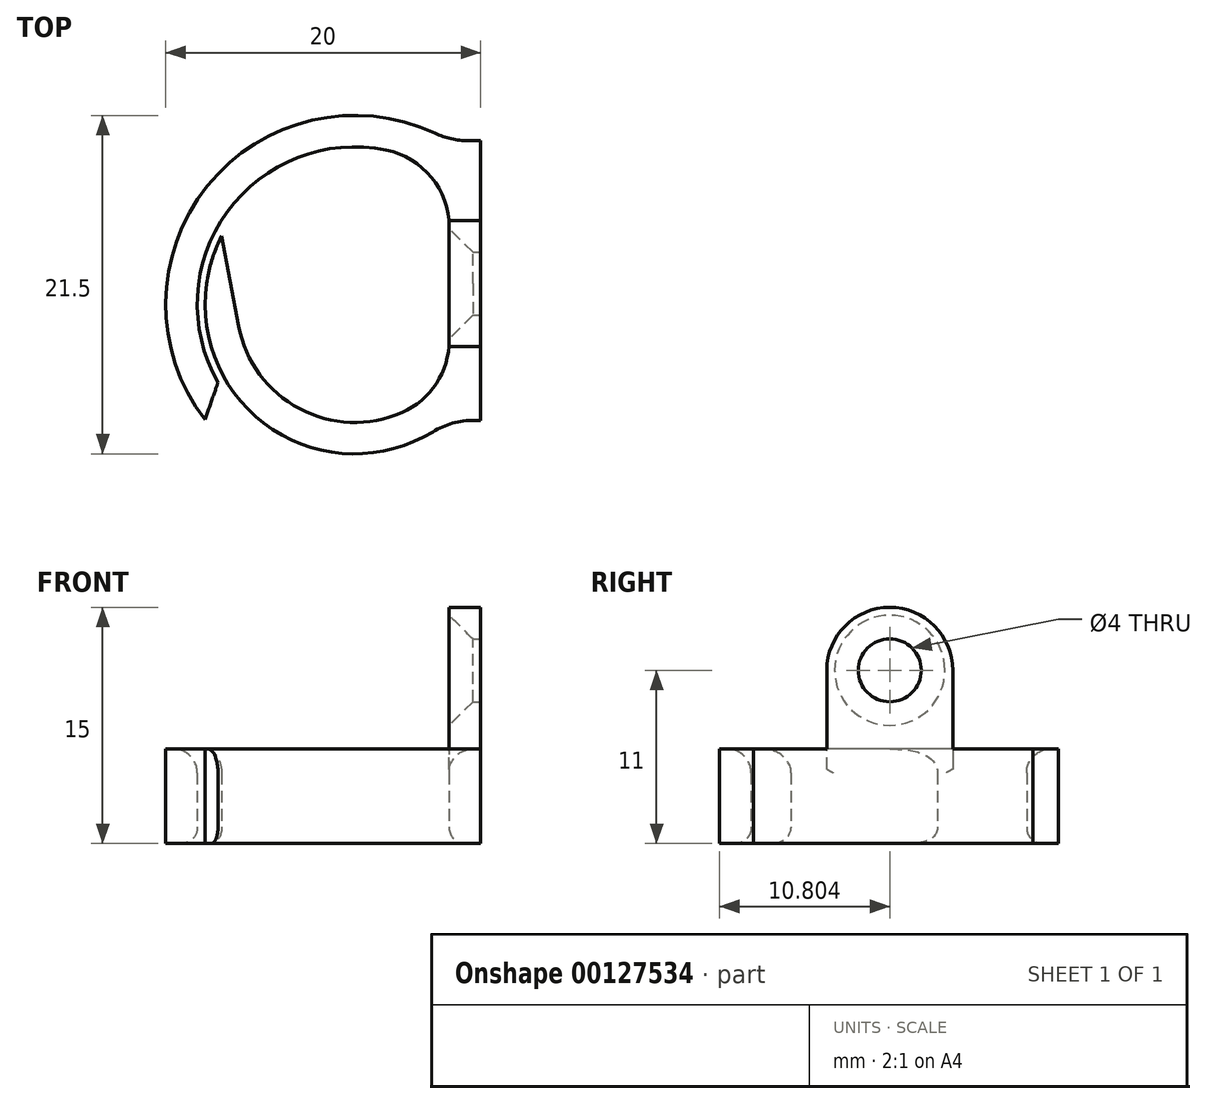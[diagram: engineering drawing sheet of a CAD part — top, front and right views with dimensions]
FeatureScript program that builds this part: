
annotation { "Feature Type Name" : "Feature", "Feature Type Description" : "" }
export const myFeature = defineFeature(function(context is Context, id is Id, definition is map)
    precondition{}
    {
        {
            var Q0;
            Q0=qCreatedBy(makeId("Top.planeOp"),FACE);
            var sketch = newSketch(context, id + "F0", { "sketchPlane" : qUnion([Q0])});
            skArc(sketch, "E0", {"start": v(2, 9.8) * mm, "mid": v(-8.1, 5.86) * mm, "end": v(-8.68, -4.96) * mm});
            skArc(sketch, "E1", {"start": v(5.1, 10.87) * mm, "mid": v(-9.36, 7.5) * mm, "end": v(-9.5, -7.33) * mm});
            skLineSegment(sketch, "E2", {"start": v(0, 0) * mm, "end": v(6, 0) * mm});
            skLineSegment(sketch, "E3", {"start": v(6, 0) * mm, "end": v(6, 4.9) * mm});
            skLineSegment(sketch, "E4.trimOffspring", {"start": v(6, 0) * mm, "end": v(6, -2.3) * mm});
            skPoint(sketch, "E5.orphan", {"position": v(12, 0) * mm});
            skLineSegment(sketch, "E6.0", {"start": v(8, 0) * mm, "end": v(8, 10.4) * mm});
            skLineSegment(sketch, "E6.1", {"start": v(8, 0) * mm, "end": v(8, -5.12) * mm});
            skLineSegment(sketch, "E7", {"start": v(7.22, 10.4) * mm, "end": v(8, 10.4) * mm});
            skPoint(sketch, "E8.endSnap0", {"position": v(-8, 0) * mm});
            skArc(sketch, "E9", {"start": v(-8.45, 4.34) * mm, "mid": v(-6.46, -6.96) * mm, "end": v(4.96, -8.1) * mm});
            skLineSegment(sketch, "E10", {"start": v(-9.5, -7.33) * mm, "end": v(-8.68, -4.96) * mm});
            skLineSegment(sketch, "E11", {"start": v(7.57, -7.37) * mm, "end": v(8, -7.37) * mm});
            skLineSegment(sketch, "E12", {"start": v(8, -5.12) * mm, "end": v(8, -7.37) * mm});
            skArc(sketch, "E13", {"start": v(-7.37, -1.39) * mm, "mid": v(-3.5, -6.63) * mm, "end": v(3, -6.87) * mm});
            skPoint(sketch, "E14.orphan", {"position": v(-8.04, 0) * mm});
            skLineSegment(sketch, "E15", {"start": v(-8.45, 4.34) * mm, "end": v(-7.37, -1.39) * mm});
            skPoint(sketch, "E16.visualSharp", {"position": v(6, 8) * mm});
            skArc(sketch, "E16.filletArc", {"start": v(6, 4.9) * mm, "mid": v(4.87, 8.06) * mm, "end": v(2, 9.8) * mm});
            skPoint(sketch, "E17.visualSharp", {"position": v(6, -4.5) * mm});
            skArc(sketch, "E17.filletArc", {"start": v(3, -6.87) * mm, "mid": v(5.18, -5.03) * mm, "end": v(6, -2.3) * mm});
            skPoint(sketch, "E18.visualSharp", {"position": v(6, -7.37) * mm});
            skArc(sketch, "E18.filletArc", {"start": v(7.57, -7.37) * mm, "mid": v(6.22, -7.55) * mm, "end": v(4.96, -8.1) * mm});
            skPoint(sketch, "E19.visualSharp", {"position": v(6, 10.4) * mm});
            skArc(sketch, "E19.filletArc", {"start": v(5.1, 10.87) * mm, "mid": v(6.13, 10.51) * mm, "end": v(7.22, 10.4) * mm});
            skSolve(sketch);
        }
        {
            var Q0;
            Q0=makeQuery(id+"F0.imprint","IMPRINT",FACE,{"disambiguationData":[TD([[makeQuery(id+"F0.imprint","IMPRINT",EDGE,{"derivedFrom":sQuery(id+"F0.wireOp",EDGE,"E0")}),-1.0]])]});
            extrude(context, id + "F1", {"entities" : qUnion([Q0]), "depth" : 6 * mm});
        }
        {
            var Q0;
            Q0=makeQuery(id+"F1.opExtrude","SWEPT_FACE",FACE,{"disambiguationData":[OSD([sQuery(id+"F0.wireOp",EDGE,"E6.0"),sQuery(id+"F0.wireOp",EDGE,"E6.1"),sQuery(id+"F0.wireOp",EDGE,"E12")])]});
            var sketch = newSketch(context, id + "F2", { "sketchPlane" : qUnion([Q0])});
            skPoint(sketch, "E20.endSnap0", {"position": v(1.3, 6) * mm});
            skCircle(sketch, "E21", {"center": v(1.3, 11) * mm, "radius": 2 * mm});
            skArc(sketch, "E22.0", {"start": v(5.3, 11) * mm, "mid": v(1.3, 15) * mm, "end": v(-2.7, 11) * mm});
            skLineSegment(sketch, "E23", {"start": v(1.3, 6) * mm, "end": v(-2.7, 6) * mm});
            skLineSegment(sketch, "E24", {"start": v(-2.7, 6) * mm, "end": v(-2.7, 11) * mm});
            skLineSegment(sketch, "E25", {"start": v(-0.7, 11) * mm, "end": v(3.3, 11) * mm});
            skLineSegment(sketch, "E26", {"start": v(5.3, 11) * mm, "end": v(5.3, 6) * mm});
            skLineSegment(sketch, "E27", {"start": v(5.3, 6) * mm, "end": v(-2.7, 6) * mm});
            skSolve(sketch);
        }
        {
            var Q0;
            Q0=makeQuery(id+"F2.imprint","IMPRINT",FACE,{"disambiguationData":[TD([[makeQuery(id+"F2.imprint","IMPRINT",EDGE,{"derivedFrom":sQuery(id+"F2.wireOp",EDGE,"E22.0")}),1.0]])]});
            extrude(context, id + "F3", {"entities" : qUnion([Q0]), "operationType" : NewBodyOperationType.ADD, "oppositeDirection" : true, "depth" : 2 * mm});
        }
        {
            var Q0;
            Q0=makeQuery(id+"F3.opExtrude","CAP_EDGE",EDGE,{"disambiguationData":[OSD([sQuery(id+"F2.wireOp",EDGE,"E21")])],"isStart":false});
            chamfer(context, id + "F4", {"entities" : qUnion([Q0]), "width" : 1.5 * mm, "tangentPropagation" : true});
        }
        {
            var Q0;
            Q0=makeQuery(id+"F1.opExtrude","CAP_EDGE",EDGE,{"disambiguationData":[OSD([sQuery(id+"F0.wireOp",EDGE,"E16.filletArc")])],"isStart":false});
            fillet(context, id + "F5", {"entities" : qUnion([Q0]), "radius" : 1.5 * mm, "tangentPropagation" : true, "allowEdgeOverflow" : false});
        }
        {
            var Q0;
            Q0=makeQuery(id+"F1.opExtrude","CAP_EDGE",EDGE,{"disambiguationData":[OSD([sQuery(id+"F0.wireOp",EDGE,"E17.filletArc")])],"isStart":false});
            fillet(context, id + "F6", {"entities" : qUnion([Q0]), "radius" : 1.5 * mm, "tangentPropagation" : true, "allowEdgeOverflow" : false});
        }
        {
            var Q0;
            Q0=makeQuery(id+"F1.opExtrude","CAP_EDGE",EDGE,{"disambiguationData":[OSD([sQuery(id+"F0.wireOp",EDGE,"E16.filletArc")])],"isStart":true});
            fillet(context, id + "F7", {"entities" : qUnion([Q0]), "radius" : 1 * mm, "tangentPropagation" : true, "allowEdgeOverflow" : false});
        }
    });
